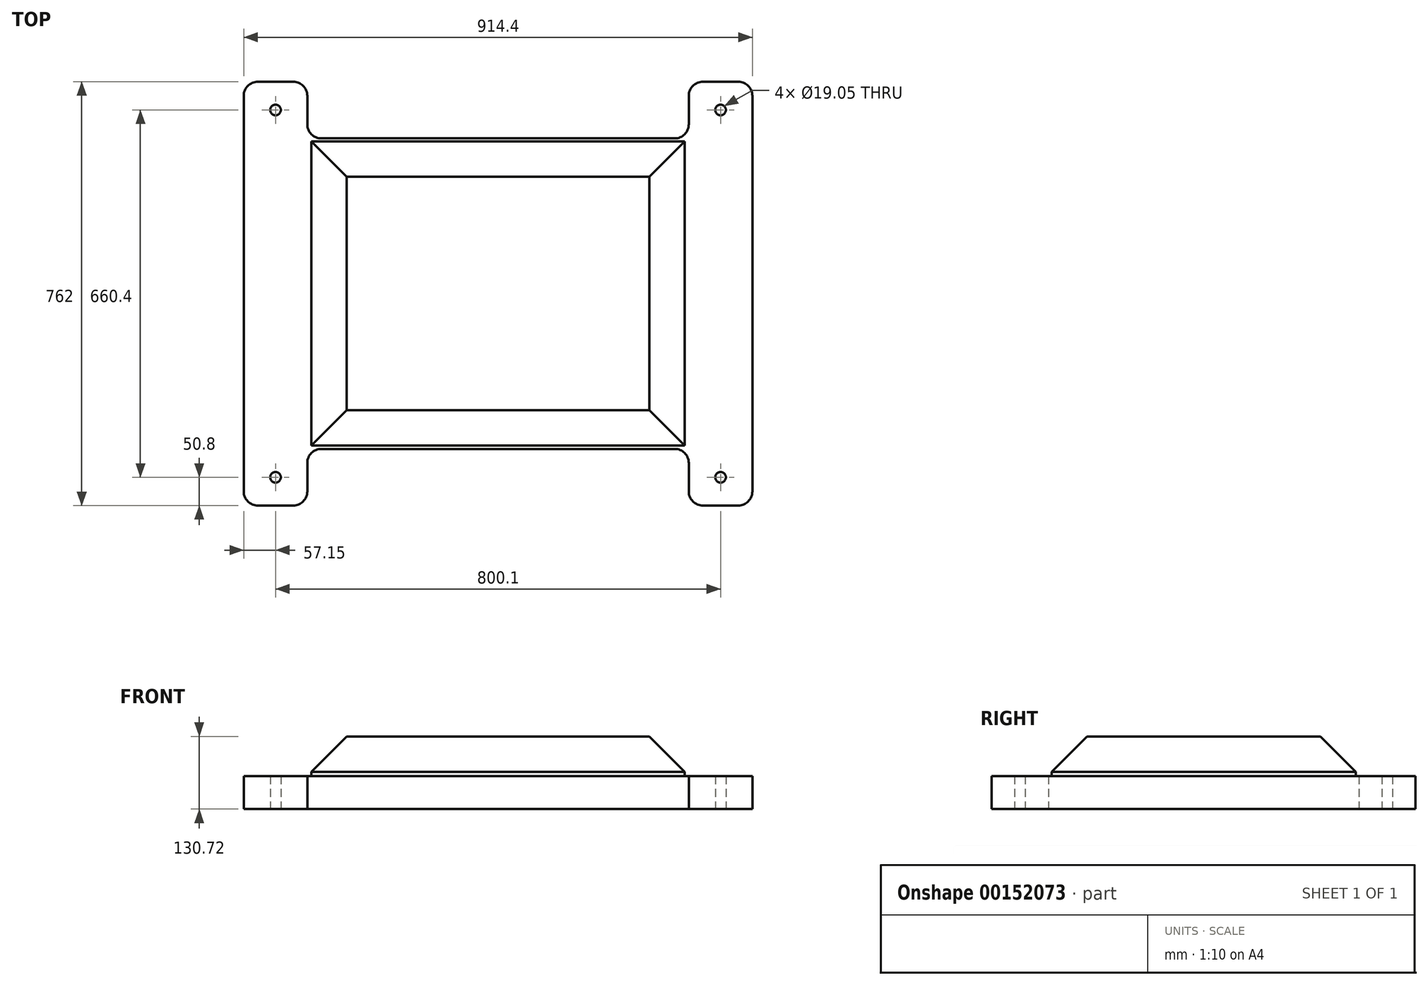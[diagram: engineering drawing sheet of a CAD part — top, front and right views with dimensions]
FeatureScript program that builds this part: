
annotation { "Feature Type Name" : "Feature", "Feature Type Description" : "" }
export const myFeature = defineFeature(function(context is Context, id is Id, definition is map)
    precondition{}
    {
        {
            var Q0;
            Q0=qCreatedBy(makeId("Top.planeOp"),FACE);
            var sketch = newSketch(context, id + "F0", { "sketchPlane" : qUnion([Q0])});
            skPoint(sketch, "E0.middle", {"position": v(0, 0) * mm});
            skLineSegment(sketch, "E1.bottom", {"start": v(457.2, 381) * mm, "end": v(342.9, 381) * mm});
            skLineSegment(sketch, "E1.top", {"start": v(457.2, -381) * mm, "end": v(342.9, -381) * mm});
            skLineSegment(sketch, "E1.left", {"start": v(457.2, 381) * mm, "end": v(457.2, -381) * mm});
            skLineSegment(sketch, "E1.right", {"start": v(-457.2, 381) * mm, "end": v(-457.2, -381) * mm});
            skCircle(sketch, "E2", {"center": v(-400.05, -330.2) * mm, "radius": 9.53 * mm});
            skCircle(sketch, "E3", {"center": v(400.05, -330.2) * mm, "radius": 9.53 * mm});
            skCircle(sketch, "E4", {"center": v(-400.05, 330.2) * mm, "radius": 9.53 * mm});
            skCircle(sketch, "E5", {"center": v(400.05, 330.2) * mm, "radius": 9.53 * mm});
            skLineSegment(sketch, "E6.left", {"start": v(-342.9, 381) * mm, "end": v(-342.9, -381) * mm});
            skLineSegment(sketch, "E6.right", {"start": v(342.9, 381) * mm, "end": v(342.9, -381) * mm});
            skLineSegment(sketch, "E7.bottom", {"start": v(-342.9, 279.13) * mm, "end": v(342.9, 279.13) * mm});
            skLineSegment(sketch, "E7.top", {"start": v(-342.9, -279.13) * mm, "end": v(342.9, -279.13) * mm});
            skLineSegment(sketch, "E7.left", {"start": v(-342.9, 279.13) * mm, "end": v(-342.9, -279.13) * mm});
            skLineSegment(sketch, "E7.right", {"start": v(342.9, 279.13) * mm, "end": v(342.9, -279.13) * mm});
            skLineSegment(sketch, "E8.trimOffspring", {"start": v(-342.9, 381) * mm, "end": v(-457.2, 381) * mm});
            skLineSegment(sketch, "E9.trimOffspring", {"start": v(-342.9, -381) * mm, "end": v(-457.2, -381) * mm});
            skSolve(sketch);
        }
        {
            var Q0;
            Q0 = qSketchRegion(id + "F0", true);
            extrude(context, id + "F1", {"entities" : qUnion([Q0]), "depth" : 38.1 * mm});
        }
        {
            var Q0;
            Q0=makeQuery(id+"F1.opExtrude","SWEPT_EDGE",EDGE,{"disambiguationData":[OSD([sQuery(id+"F0.wireOp",EDGE,"E1.right"),sQuery(id+"F0.wireOp",EDGE,"E9.trimOffspring")])]});
            var Q1;
            Q1=makeQuery(id+"F1.opExtrude","SWEPT_EDGE",EDGE,{"disambiguationData":[OSD([sQuery(id+"F0.wireOp",EDGE,"E6.left"),sQuery(id+"F0.wireOp",EDGE,"E9.trimOffspring")])]});
            var Q2;
            Q2=makeQuery(id+"F1.opExtrude","SWEPT_EDGE",EDGE,{"disambiguationData":[OSD([sQuery(id+"F0.wireOp",EDGE,"E1.top"),sQuery(id+"F0.wireOp",EDGE,"E6.right")])]});
            var Q3;
            Q3=makeQuery(id+"F1.opExtrude","SWEPT_EDGE",EDGE,{"disambiguationData":[OSD([sQuery(id+"F0.wireOp",EDGE,"E1.top"),sQuery(id+"F0.wireOp",EDGE,"E1.left")])]});
            var Q4;
            Q4=makeQuery(id+"F1.opExtrude","SWEPT_EDGE",EDGE,{"disambiguationData":[OSD([sQuery(id+"F0.wireOp",EDGE,"E1.bottom"),sQuery(id+"F0.wireOp",EDGE,"E6.right")])]});
            var Q5;
            Q5=makeQuery(id+"F1.opExtrude","SWEPT_EDGE",EDGE,{"disambiguationData":[OSD([sQuery(id+"F0.wireOp",EDGE,"E1.right"),sQuery(id+"F0.wireOp",EDGE,"E8.trimOffspring")])]});
            var Q6;
            Q6=makeQuery(id+"F1.opExtrude","SWEPT_EDGE",EDGE,{"disambiguationData":[OSD([sQuery(id+"F0.wireOp",EDGE,"E6.left"),sQuery(id+"F0.wireOp",EDGE,"E7.top"),sQuery(id+"F0.wireOp",EDGE,"E7.left")])]});
            var Q7;
            Q7=makeQuery(id+"F1.opExtrude","SWEPT_EDGE",EDGE,{"disambiguationData":[OSD([sQuery(id+"F0.wireOp",EDGE,"E6.right"),sQuery(id+"F0.wireOp",EDGE,"E7.top"),sQuery(id+"F0.wireOp",EDGE,"E7.right")])]});
            var Q8;
            Q8=makeQuery(id+"F1.opExtrude","SWEPT_EDGE",EDGE,{"disambiguationData":[OSD([sQuery(id+"F0.wireOp",EDGE,"E1.bottom"),sQuery(id+"F0.wireOp",EDGE,"E1.left")])]});
            var Q9;
            Q9=makeQuery(id+"F1.opExtrude","SWEPT_EDGE",EDGE,{"disambiguationData":[OSD([sQuery(id+"F0.wireOp",EDGE,"E6.left"),sQuery(id+"F0.wireOp",EDGE,"E7.bottom"),sQuery(id+"F0.wireOp",EDGE,"E7.left")])]});
            var Q10;
            Q10=makeQuery(id+"F1.opExtrude","SWEPT_EDGE",EDGE,{"disambiguationData":[OSD([sQuery(id+"F0.wireOp",EDGE,"E6.left"),sQuery(id+"F0.wireOp",EDGE,"E8.trimOffspring")])]});
            var Q11;
            Q11=makeQuery(id+"F1.opExtrude","SWEPT_EDGE",EDGE,{"disambiguationData":[OSD([sQuery(id+"F0.wireOp",EDGE,"E6.right"),sQuery(id+"F0.wireOp",EDGE,"E7.bottom"),sQuery(id+"F0.wireOp",EDGE,"E7.right")])]});
            fillet(context, id + "F2", {"entities" : qUnion([Q0, Q1, Q2, Q3, Q4, Q5, Q6, Q7, Q8, Q9, Q10, Q11]), "radius" : 25.4 * mm, "tangentPropagation" : true, "allowEdgeOverflow" : false});
        }
        {
            var Q0;
            Q0=makeQuery(id+"F1.opExtrude","CAP_FACE",FACE,{"disambiguationData":[OSD([sQuery(id+"F0.wireOp",EDGE,"E1.bottom"),sQuery(id+"F0.wireOp",EDGE,"E1.top"),sQuery(id+"F0.wireOp",EDGE,"E1.left"),sQuery(id+"F0.wireOp",EDGE,"E1.right"),sQuery(id+"F0.wireOp",EDGE,"E2"),sQuery(id+"F0.wireOp",EDGE,"E3"),sQuery(id+"F0.wireOp",EDGE,"E4"),sQuery(id+"F0.wireOp",EDGE,"E5"),sQuery(id+"F0.wireOp",EDGE,"E6.left"),sQuery(id+"F0.wireOp",EDGE,"E6.right"),sQuery(id+"F0.wireOp",EDGE,"E7.bottom"),sQuery(id+"F0.wireOp",EDGE,"E7.top"),sQuery(id+"F0.wireOp",EDGE,"E8.trimOffspring"),sQuery(id+"F0.wireOp",EDGE,"E9.trimOffspring")])],"isStart":false});
            var sketch = newSketch(context, id + "F3", { "sketchPlane" : qUnion([Q0])});
            skLineSegment(sketch, "E10.bottom", {"start": v(-335.46, -273.36) * mm, "end": v(335.46, -273.36) * mm});
            skLineSegment(sketch, "E10.top", {"start": v(-335.46, 273.36) * mm, "end": v(335.46, 273.36) * mm});
            skLineSegment(sketch, "E10.left", {"start": v(-335.46, -273.36) * mm, "end": v(-335.46, 273.36) * mm});
            skLineSegment(sketch, "E10.right", {"start": v(335.46, -273.36) * mm, "end": v(335.46, 273.36) * mm});
            skPoint(sketch, "E10.middle", {"position": v(0, 0) * mm});
            skPoint(sketch, "E10.cornerSnap0", {"position": v(-335.46, -286.57) * mm});
            skSolve(sketch);
        }
        {
            var Q0;
            Q0 = qSketchRegion(id + "F3", true);
            extrude(context, id + "F4", {"entities" : qUnion([Q0]), "operationType" : NewBodyOperationType.ADD, "depth" : 71.12 * mm});
        }
        {
            var Q0;
            Q0=makeQuery(id+"F4.opExtrude","CAP_EDGE",EDGE,{"disambiguationData":[OSD([sQuery(id+"F3.wireOp",EDGE,"E10.top")])],"isStart":false});
            var Q1;
            Q1=makeQuery(id+"F4.opExtrude","CAP_EDGE",EDGE,{"disambiguationData":[OSD([sQuery(id+"F3.wireOp",EDGE,"E10.right")])],"isStart":false});
            var Q2;
            Q2=makeQuery(id+"F4.opExtrude","CAP_EDGE",EDGE,{"disambiguationData":[OSD([sQuery(id+"F3.wireOp",EDGE,"E10.left")])],"isStart":false});
            var Q3;
            Q3=makeQuery(id+"F4.opExtrude","CAP_EDGE",EDGE,{"disambiguationData":[OSD([sQuery(id+"F3.wireOp",EDGE,"E10.bottom")])],"isStart":false});
            chamfer(context, id + "F5", {"entities" : qUnion([Q0, Q1, Q2, Q3]), "width" : 63.5 * mm, "tangentPropagation" : true});
        }
        {
            var Q0;
            Q0=makeQuery(id+"F1.opExtrude","CAP_FACE",FACE,{"disambiguationData":[OSD([sQuery(id+"F0.wireOp",EDGE,"E1.bottom"),sQuery(id+"F0.wireOp",EDGE,"E1.top"),sQuery(id+"F0.wireOp",EDGE,"E1.left"),sQuery(id+"F0.wireOp",EDGE,"E1.right"),sQuery(id+"F0.wireOp",EDGE,"E2"),sQuery(id+"F0.wireOp",EDGE,"E3"),sQuery(id+"F0.wireOp",EDGE,"E4"),sQuery(id+"F0.wireOp",EDGE,"E5"),sQuery(id+"F0.wireOp",EDGE,"E6.left"),sQuery(id+"F0.wireOp",EDGE,"E6.right"),sQuery(id+"F0.wireOp",EDGE,"E7.bottom"),sQuery(id+"F0.wireOp",EDGE,"E7.top"),sQuery(id+"F0.wireOp",EDGE,"E8.trimOffspring"),sQuery(id+"F0.wireOp",EDGE,"E9.trimOffspring")])],"isStart":true});
            extrude(context, id + "F6", {"entities" : qUnion([Q0]), "operationType" : NewBodyOperationType.ADD, "depth" : 21.5 * mm});
        }
    });
